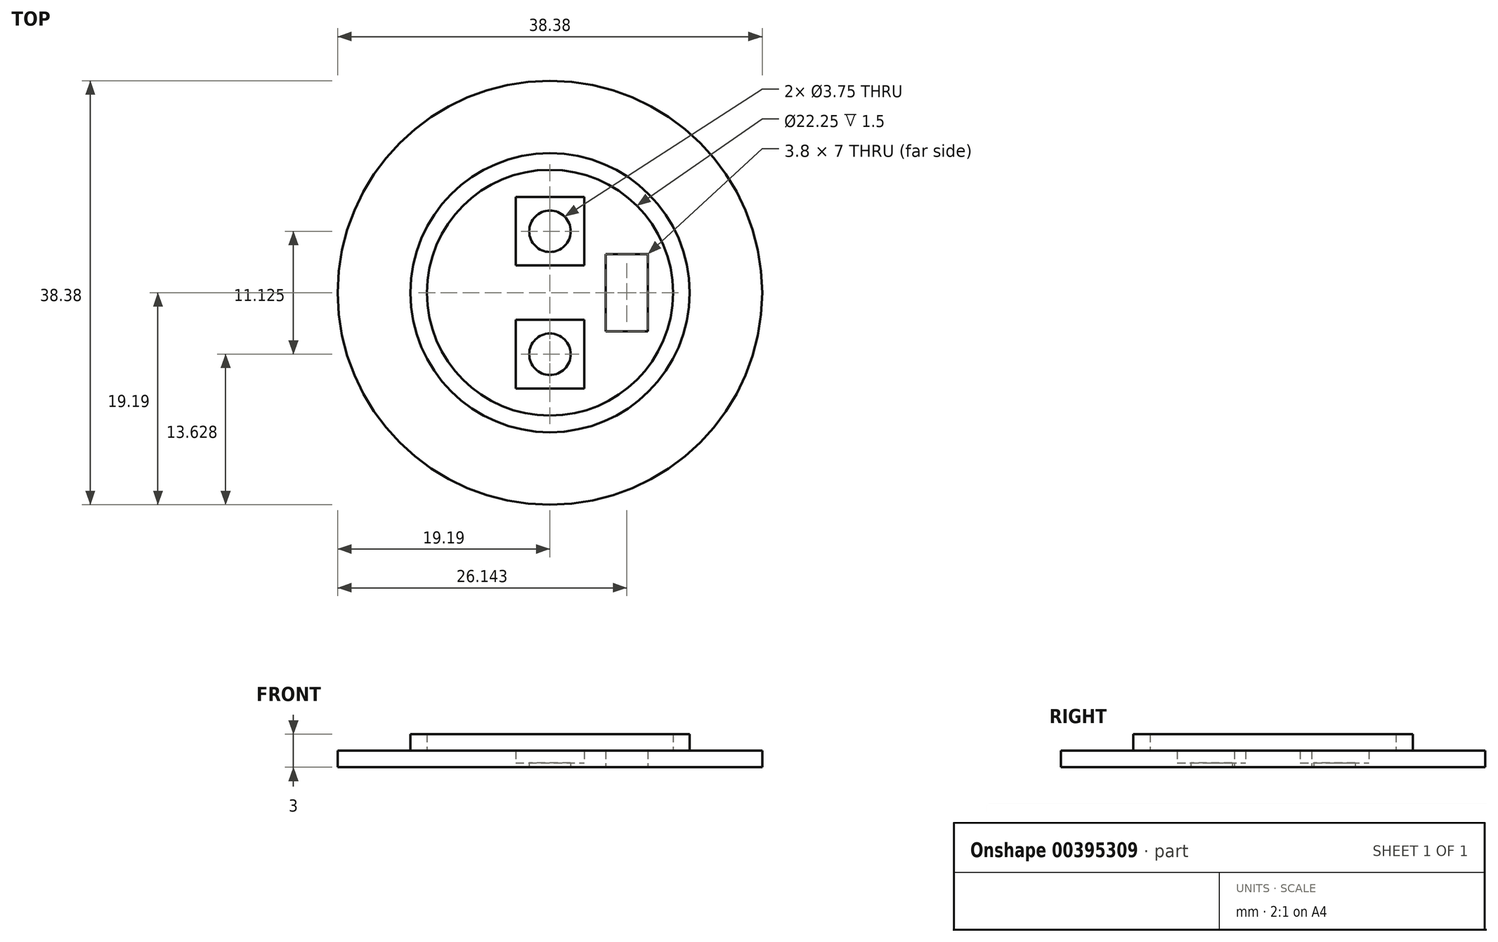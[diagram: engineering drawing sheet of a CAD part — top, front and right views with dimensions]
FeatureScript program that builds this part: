
annotation { "Feature Type Name" : "Feature", "Feature Type Description" : "" }
export const myFeature = defineFeature(function(context is Context, id is Id, definition is map)
    precondition{}
    {
        {
            var Q0;
            Q0=qCreatedBy(makeId("Top.planeOp"),FACE);
            var sketch = newSketch(context, id + "F0", { "sketchPlane" : qUnion([Q0])});
            skCircle(sketch, "E0", {"center": v(0, 0) * mm, "radius": 12.62 * mm});
            skCircle(sketch, "E1", {"center": v(0, 0) * mm, "radius": 19.19 * mm});
            skCircle(sketch, "E2", {"center": v(0, 0) * mm, "radius": 11.13 * mm});
            skLineSegment(sketch, "E3", {"start": v(0, 11.13) * mm, "end": v(0, -11.13) * mm});
            skLineSegment(sketch, "E4", {"start": v(0, 11.13) * mm, "end": v(0, 0) * mm, "construction": true});
            skLineSegment(sketch, "E5", {"start": v(0, 5.56) * mm, "end": v(0, 11.13) * mm, "construction": true});
            skLineSegment(sketch, "E6", {"start": v(0, 0) * mm, "end": v(0, -11.13) * mm, "construction": true});
            skLineSegment(sketch, "E7", {"start": v(0, -5.56) * mm, "end": v(0, 0) * mm, "construction": true});
            skCircle(sketch, "E8", {"center": v(0, 5.56) * mm, "radius": 1.88 * mm});
            skCircle(sketch, "E9", {"center": v(0, -5.56) * mm, "radius": 1.88 * mm});
            skLineSegment(sketch, "E10", {"start": v(0, 0) * mm, "end": v(11.13, 0) * mm, "construction": true});
            skLineSegment(sketch, "E11", {"start": v(11.13, 0) * mm, "end": v(5.56, 0) * mm, "construction": true});
            skLineSegment(sketch, "E12", {"start": v(0, 5.56) * mm, "end": v(-3.1, 5.56) * mm});
            skLineSegment(sketch, "E13", {"start": v(0, 5.56) * mm, "end": v(0, 8.34) * mm});
            skLineSegment(sketch, "E14", {"start": v(0, 5.56) * mm, "end": v(0, 2.46) * mm});
            skLineSegment(sketch, "E15", {"start": v(0, 2.46) * mm, "end": v(-3.1, 2.46) * mm});
            skLineSegment(sketch, "E16", {"start": v(-3.1, 5.56) * mm, "end": v(-3.1, 8.66) * mm});
            skLineSegment(sketch, "E17", {"start": v(-3.1, 8.66) * mm, "end": v(3.1, 8.66) * mm});
            skLineSegment(sketch, "E18", {"start": v(3.1, 8.66) * mm, "end": v(3.1, 2.46) * mm});
            skLineSegment(sketch, "E19", {"start": v(3.1, 2.46) * mm, "end": v(0, 2.46) * mm});
            skLineSegment(sketch, "E20", {"start": v(-3.1, 5.56) * mm, "end": v(-3.1, 2.46) * mm});
            skLineSegment(sketch, "E21", {"start": v(5.56, 0) * mm, "end": v(8.34, 0) * mm, "construction": true});
            skLineSegment(sketch, "E22", {"start": v(8.34, 0) * mm, "end": v(6.95, 0) * mm, "construction": true});
            skLineSegment(sketch, "E23", {"start": v(6.95, 0) * mm, "end": v(8.34, 0) * mm, "construction": true});
            skLineSegment(sketch, "E24", {"start": v(6.95, 0) * mm, "end": v(6.95, -3.5) * mm});
            skLineSegment(sketch, "E25", {"start": v(6.95, -3.5) * mm, "end": v(8.85, -3.5) * mm});
            skLineSegment(sketch, "E26", {"start": v(8.85, -3.5) * mm, "end": v(8.85, 3.5) * mm});
            skLineSegment(sketch, "E27", {"start": v(8.85, 3.5) * mm, "end": v(6.95, 3.5) * mm});
            skLineSegment(sketch, "E28", {"start": v(6.95, 3.5) * mm, "end": v(5.05, 3.5) * mm});
            skLineSegment(sketch, "E29", {"start": v(5.05, 3.5) * mm, "end": v(5.05, -3.5) * mm});
            skLineSegment(sketch, "E30", {"start": v(5.05, -3.5) * mm, "end": v(6.95, -3.5) * mm});
            skLineSegment(sketch, "E31", {"start": v(0, -5.56) * mm, "end": v(0, -2.46) * mm});
            skLineSegment(sketch, "E32", {"start": v(0, -2.46) * mm, "end": v(-3.1, -2.46) * mm});
            skLineSegment(sketch, "E33", {"start": v(-3.1, -2.46) * mm, "end": v(-3.1, -8.66) * mm});
            skLineSegment(sketch, "E34", {"start": v(-3.1, -8.66) * mm, "end": v(3.1, -8.66) * mm});
            skLineSegment(sketch, "E35", {"start": v(3.1, -8.66) * mm, "end": v(3.1, -2.46) * mm});
            skLineSegment(sketch, "E36", {"start": v(3.1, -2.46) * mm, "end": v(0, -2.46) * mm});
            skSolve(sketch);
        }
        {
            var Q0;
            Q0=makeQuery(id+"F0.imprint","IMPRINT",FACE,{"disambiguationData":[TD([[makeQuery(id+"F0.imprint","IMPRINT",EDGE,{"derivedFrom":sQuery(id+"F0.wireOp",EDGE,"E0")}),-1.0]])]});
            extrude(context, id + "F1", {"entities" : qUnion([Q0]), "depth" : 1.5 * mm});
        }
        {
            var Q0;
            Q0=makeQuery(id+"F0.imprint","IMPRINT",FACE,{"disambiguationData":[TD([[makeQuery(id+"F0.imprint","IMPRINT",EDGE,{"derivedFrom":sQuery(id+"F0.wireOp",EDGE,"E0")}),1.0]])]});
            extrude(context, id + "F2", {"entities" : qUnion([Q0]), "operationType" : NewBodyOperationType.ADD, "depth" : 3 * mm});
        }
        {
            var Q0;
            {var subQ7=sQuery(id+"F0.wireOp",EDGE,"E15");Q0=makeQuery(id+"F0.imprint","IMPRINT",FACE,{"disambiguationData":[TD([[makeQuery(id+"F0.imprint","IMPRINT",EDGE,{"derivedFrom":subQ7}),1.0]])]});}
            var Q1;
            {var subQ0=sQuery(id+"F0.wireOp",EDGE,"E18");Q1=makeQuery(id+"F0.imprint","IMPRINT",FACE,{"disambiguationData":[TD([[makeQuery(id+"F0.imprint","IMPRINT",EDGE,{"derivedFrom":subQ0}),1.0]])]});}
            extrude(context, id + "F3", {"entities" : qUnion([Q0, Q1]), "operationType" : NewBodyOperationType.ADD, "depth" : 1.5 * mm});
        }
        {
            var Q0;
            {var subQ10=sQuery(id+"F0.wireOp",EDGE,"E18");Q0=makeQuery(id+"F0.imprint","IMPRINT",FACE,{"disambiguationData":[TD([[makeQuery(id+"F0.imprint","IMPRINT",EDGE,{"derivedFrom":subQ10}),-1.0]])]});}
            var Q1;
            {var subQ5=sQuery(id+"F0.wireOp",EDGE,"E16");Q1=makeQuery(id+"F0.imprint","IMPRINT",FACE,{"disambiguationData":[TD([[makeQuery(id+"F0.imprint","IMPRINT",EDGE,{"derivedFrom":subQ5}),-1.0]])]});}
            var Q2;
            {var subQ0=sQuery(id+"F0.wireOp",EDGE,"E15");Q2=makeQuery(id+"F0.imprint","IMPRINT",FACE,{"disambiguationData":[TD([[makeQuery(id+"F0.imprint","IMPRINT",EDGE,{"derivedFrom":subQ0}),-1.0]])]});}
            var Q3;
            {var subQ5=sQuery(id+"F0.wireOp",EDGE,"E35");Q3=makeQuery(id+"F0.imprint","IMPRINT",FACE,{"disambiguationData":[TD([[makeQuery(id+"F0.imprint","IMPRINT",EDGE,{"derivedFrom":subQ5}),1.0]])]});}
            var Q4;
            {var subQ0=sQuery(id+"F0.wireOp",EDGE,"E32");Q4=makeQuery(id+"F0.imprint","IMPRINT",FACE,{"disambiguationData":[TD([[makeQuery(id+"F0.imprint","IMPRINT",EDGE,{"derivedFrom":subQ0}),1.0]])]});}
            extrude(context, id + "F4", {"entities" : qUnion([Q0, Q1, Q2, Q3, Q4]), "operationType" : NewBodyOperationType.ADD, "depth" : .4 * mm});
        }
    });
